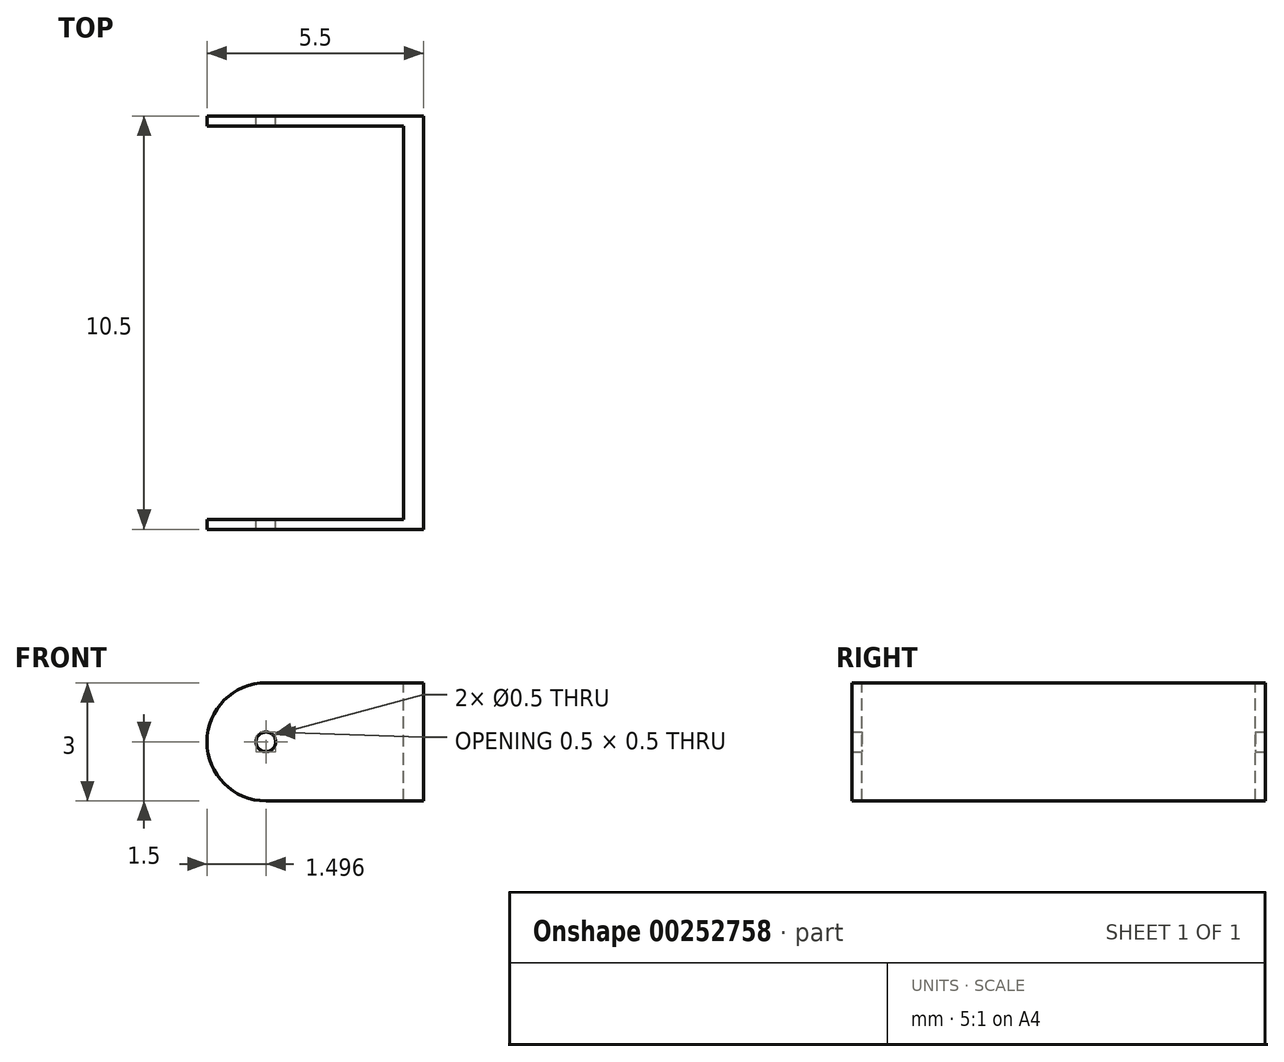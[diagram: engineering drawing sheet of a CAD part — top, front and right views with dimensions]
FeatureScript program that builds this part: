
annotation { "Feature Type Name" : "Feature", "Feature Type Description" : "" }
export const myFeature = defineFeature(function(context is Context, id is Id, definition is map)
    precondition{}
    {
        {
            var Q0;
            Q0=qCreatedBy(makeId("Front.planeOp"),FACE);
            var sketch = newSketch(context, id + "F0", { "sketchPlane" : qUnion([Q0])});
            skLineSegment(sketch, "E0.bottom", {"start": v(-0.71, 1.5) * mm, "end": v(3.29, 1.5) * mm});
            skLineSegment(sketch, "E0.top", {"start": v(-0.71, -1.5) * mm, "end": v(3.29, -1.5) * mm});
            skLineSegment(sketch, "E0.left", {"start": v(-0.71, 1.5) * mm, "end": v(-0.71, -1.5) * mm});
            skLineSegment(sketch, "E0.right", {"start": v(3.29, 1.5) * mm, "end": v(3.29, -1.5) * mm});
            skPoint(sketch, "E0.middle", {"position": v(1.29, 0) * mm});
            skCircle(sketch, "E1", {"center": v(-0.71, 0) * mm, "radius": 1.5 * mm});
            skCircle(sketch, "E2", {"center": v(-0.71, 0) * mm, "radius": 0.25 * mm});
            skSolve(sketch);
        }
        {
            var Q0;
            {var subQ0=sQuery(id+"F0.wireOp",EDGE,"E0.bottom");Q0=makeQuery(id+"F0.imprint","IMPRINT",FACE,{"disambiguationData":[TD([[makeQuery(id+"F0.imprint","IMPRINT",EDGE,{"derivedFrom":subQ0}),-1.0]])]});}
            var Q1;
            {var subQ1=sQuery(id+"F0.wireOp",EDGE,"E0.left");var subQ3=sQuery(id+"F0.wireOp",EDGE,"E2");var subQ4=makeQuery(id+"F0.imprint","INTERSECT",VERTEX,{"disambiguationData":[OD(0.0)],"derivedFrom":[subQ1,subQ3]});Q1=makeQuery(id+"F0.imprint","IMPRINT",FACE,{"disambiguationData":[TD([[makeQuery(id+"F0.imprint","IMPRINT",EDGE,{"disambiguationData":[TD([[subQ4,1.0]])],"derivedFrom":subQ3}),-1.0]])]});}
            var Q2;
            {var subQ1=sQuery(id+"F0.wireOp",EDGE,"E0.left");var subQ3=sQuery(id+"F0.wireOp",EDGE,"E2");var subQ4=makeQuery(id+"F0.imprint","INTERSECT",VERTEX,{"disambiguationData":[OD(0.0)],"derivedFrom":[subQ1,subQ3]});Q2=makeQuery(id+"F0.imprint","IMPRINT",FACE,{"disambiguationData":[TD([[makeQuery(id+"F0.imprint","IMPRINT",EDGE,{"disambiguationData":[TD([[subQ4,-1.0]])],"derivedFrom":subQ3}),-1.0]])]});}
            extrude(context, id + "F1", {"entities" : qUnion([Q0, Q1, Q2]), "endBound" : BoundingType.SYMMETRIC, "depth" : 10.5 * mm});
        }
        {
            var Q0;
            Q0=makeQuery(id+"F1.opExtrude","SWEPT_FACE",FACE,{"disambiguationData":[OSD([sQuery(id+"F0.wireOp",EDGE,"E0.bottom")])]});
            var sketch = newSketch(context, id + "F2", { "sketchPlane" : qUnion([Q0])});
            skLineSegment(sketch, "E3.bottom", {"start": v(3.29, -5.25) * mm, "end": v(2.79, -5.25) * mm});
            skLineSegment(sketch, "E3.top", {"start": v(3.29, -5) * mm, "end": v(2.79, -5) * mm});
            skLineSegment(sketch, "E3.left", {"start": v(3.29, -5.25) * mm, "end": v(3.29, -5) * mm});
            skLineSegment(sketch, "E3.right", {"start": v(2.79, -5.25) * mm, "end": v(2.79, -5) * mm});
            skLineSegment(sketch, "E4.MirrorCS", {"start": v(3.29, 5) * mm, "end": v(2.79, 5) * mm});
            skLineSegment(sketch, "E5.MirrorCS", {"start": v(2.79, 5.25) * mm, "end": v(2.79, 5) * mm});
            skLineSegment(sketch, "E6.MirrorCS", {"start": v(3.29, 5.25) * mm, "end": v(2.79, 5.25) * mm});
            skLineSegment(sketch, "E7.MirrorCS", {"start": v(3.29, 5.25) * mm, "end": v(3.29, 5) * mm});
            skLineSegment(sketch, "E8.bottom", {"start": v(2.79, -5) * mm, "end": v(-3.02, -5) * mm});
            skLineSegment(sketch, "E8.top", {"start": v(2.79, 5) * mm, "end": v(-3.02, 5) * mm});
            skLineSegment(sketch, "E8.left", {"start": v(2.79, -5) * mm, "end": v(2.79, 5) * mm});
            skLineSegment(sketch, "E8.right", {"start": v(-3.02, -5) * mm, "end": v(-3.02, 5) * mm});
            skSolve(sketch);
        }
        {
            var Q0;
            {var subQ0=sQuery(id+"F2.wireOp",EDGE,"E8.left");Q0=makeQuery(id+"F2.imprint","IMPRINT",FACE,{"disambiguationData":[TD([[makeQuery(id+"F2.imprint","IMPRINT",EDGE,{"derivedFrom":subQ0}),1.0]])]});}
            var Q1;
            {var subQ0=sQuery(id+"F2.wireOp",EDGE,"E8.right");Q1=makeQuery(id+"F2.imprint","IMPRINT",FACE,{"disambiguationData":[TD([[makeQuery(id+"F2.imprint","IMPRINT",EDGE,{"derivedFrom":subQ0}),-1.0]])]});}
            extrude(context, id + "F3", {"entities" : qUnion([Q0, Q1]), "operationType" : NewBodyOperationType.REMOVE, "endBound" : BoundingType.SYMMETRIC, "oppositeDirection" : true, "depth" : 10 * mm});
        }
    });
